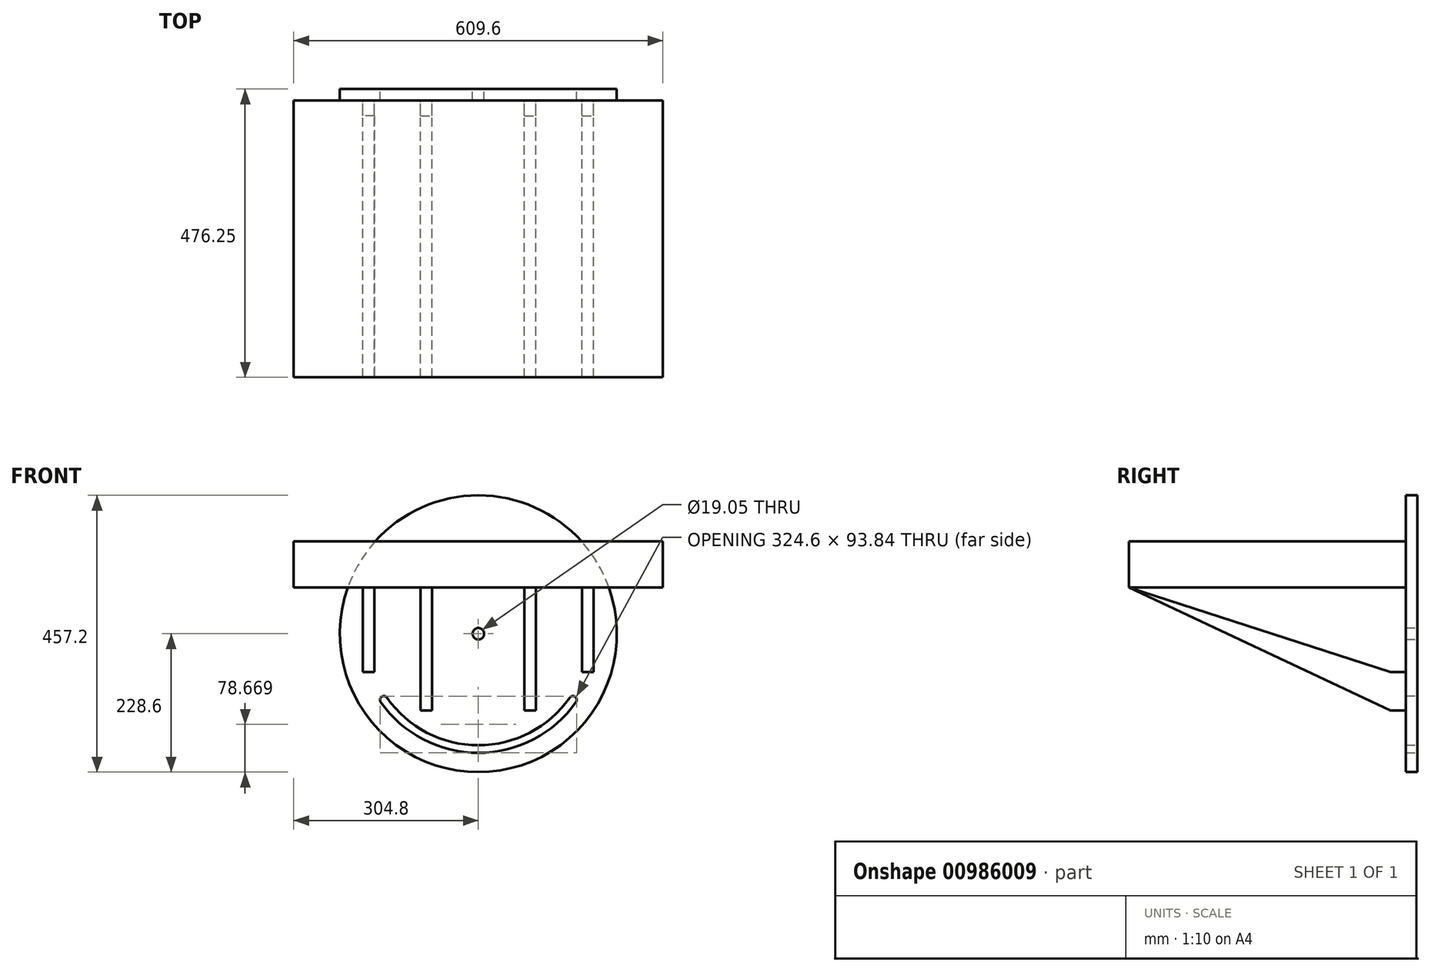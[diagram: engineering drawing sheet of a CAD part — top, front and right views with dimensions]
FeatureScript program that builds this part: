
annotation { "Feature Type Name" : "Feature", "Feature Type Description" : "" }
export const myFeature = defineFeature(function(context is Context, id is Id, definition is map)
    precondition{}
    {
        {
            var Q0;
            Q0=qCreatedBy(makeId("Front.planeOp"),FACE);
            var sketch = newSketch(context, id + "F0", { "sketchPlane" : qUnion([Q0])});
            skCircle(sketch, "E0", {"center": v(0, 0) * mm, "radius": 228.6 * mm});
            skCircle(sketch, "E1", {"center": v(0, 0) * mm, "radius": 9.53 * mm});
            skArc(sketch, "E2.0", {"start": v(-156.05, -109.27) * mm, "mid": v(0, -190.5) * mm, "end": v(156.05, -109.27) * mm});
            skLineSegment(sketch, "E3", {"start": v(0, 0) * mm, "end": v(0, -9.53) * mm});
            skLineSegment(sketch, "E4", {"start": v(0, 0) * mm, "end": v(7.8, -5.46) * mm});
            skLineSegment(sketch, "E5", {"start": v(0, 0) * mm, "end": v(-7.8, -5.46) * mm});
            skArc(sketch, "E6.0.startCap", {"start": v(-161.25, -112.9) * mm, "mid": v(-159.7, -104.06) * mm, "end": v(-150.85, -105.62) * mm});
            skArc(sketch, "E6.0.endCap", {"start": v(150.85, -105.62) * mm, "mid": v(159.7, -104.06) * mm, "end": v(161.25, -112.9) * mm});
            skArc(sketch, "E6.0.left", {"start": v(-150.85, -105.62) * mm, "mid": v(0, -184.15) * mm, "end": v(150.85, -105.62) * mm});
            skArc(sketch, "E6.0.right", {"start": v(-161.25, -112.9) * mm, "mid": v(0, -196.85) * mm, "end": v(161.25, -112.9) * mm});
            skSolve(sketch);
        }
        {
            var Q0;
            Q0=makeQuery(id+"F0.imprint","IMPRINT",FACE,{"disambiguationData":[TD([[makeQuery(id+"F0.imprint","IMPRINT",EDGE,{"derivedFrom":sQuery(id+"F0.wireOp",EDGE,"E0")}),1.0]])]});
            extrude(context, id + "F1", {"entities" : qUnion([Q0]), "depth" : 19.05 * mm, "offsetDistance" : 25.4 * mm});
        }
        {
            var Q0;
            Q0=makeQuery(id+"F1.opExtrude","CAP_FACE",FACE,{"disambiguationData":[OSD([sQuery(id+"F0.wireOp",EDGE,"E0"),sQuery(id+"F0.wireOp",EDGE,"E1"),sQuery(id+"F0.wireOp",EDGE,"E6.0.startCap"),sQuery(id+"F0.wireOp",EDGE,"E6.0.endCap"),sQuery(id+"F0.wireOp",EDGE,"E6.0.left"),sQuery(id+"F0.wireOp",EDGE,"E6.0.right")])],"isStart":false});
            var sketch = newSketch(context, id + "F2", { "sketchPlane" : qUnion([Q0])});
            skLineSegment(sketch, "E7.bottom", {"start": v(-304.8, 152.4) * mm, "end": v(304.8, 152.4) * mm});
            skLineSegment(sketch, "E7.top", {"start": v(-304.8, 76.2) * mm, "end": v(304.8, 76.2) * mm});
            skLineSegment(sketch, "E7.left", {"start": v(-304.8, 152.4) * mm, "end": v(-304.8, 76.2) * mm});
            skLineSegment(sketch, "E7.right", {"start": v(304.8, 152.4) * mm, "end": v(304.8, 76.2) * mm});
            skPoint(sketch, "E7.middle", {"position": v(0, 114.3) * mm});
            skLineSegment(sketch, "E8.bottom", {"start": v(190.5, 76.2) * mm, "end": v(171.45, 76.2) * mm});
            skLineSegment(sketch, "E8.top", {"start": v(190.5, -63.5) * mm, "end": v(171.45, -63.5) * mm});
            skLineSegment(sketch, "E8.left", {"start": v(190.5, 76.2) * mm, "end": v(190.5, -63.5) * mm});
            skLineSegment(sketch, "E8.right", {"start": v(171.45, 76.2) * mm, "end": v(171.45, -63.5) * mm});
            skLineSegment(sketch, "E9.bottom", {"start": v(-190.5, 76.2) * mm, "end": v(-171.45, 76.2) * mm});
            skLineSegment(sketch, "E9.top", {"start": v(-190.5, -63.5) * mm, "end": v(-171.45, -63.5) * mm});
            skLineSegment(sketch, "E9.left", {"start": v(-190.5, 76.2) * mm, "end": v(-190.5, -63.5) * mm});
            skLineSegment(sketch, "E9.right", {"start": v(-171.45, 76.2) * mm, "end": v(-171.45, -63.5) * mm});
            skLineSegment(sketch, "E10.bottom", {"start": v(-95.25, 76.2) * mm, "end": v(-76.2, 76.2) * mm});
            skLineSegment(sketch, "E10.top", {"start": v(-95.25, -127) * mm, "end": v(-76.2, -127) * mm});
            skLineSegment(sketch, "E10.left", {"start": v(-95.25, 76.2) * mm, "end": v(-95.25, -127) * mm});
            skLineSegment(sketch, "E10.right", {"start": v(-76.2, 76.2) * mm, "end": v(-76.2, -127) * mm});
            skLineSegment(sketch, "E11.bottom", {"start": v(95.25, 76.2) * mm, "end": v(76.2, 76.2) * mm});
            skLineSegment(sketch, "E11.top", {"start": v(95.25, -127) * mm, "end": v(76.2, -127) * mm});
            skLineSegment(sketch, "E11.left", {"start": v(95.25, 76.2) * mm, "end": v(95.25, -127) * mm});
            skLineSegment(sketch, "E11.right", {"start": v(76.2, 76.2) * mm, "end": v(76.2, -127) * mm});
            skSolve(sketch);
        }
        {
            var Q0;
            {var subQ0=sQuery(id+"F2.wireOp",EDGE,"E7.right");Q0=makeQuery(id+"F2.imprint","IMPRINT",FACE,{"disambiguationData":[TD([[makeQuery(id+"F2.imprint","IMPRINT",EDGE,{"derivedFrom":subQ0}),-1.0]])]});}
            var Q1;
            {var subQ2=makeQuery(id+"F1.opExtrude","CAP_EDGE",EDGE,{"disambiguationData":[OSD([sQuery(id+"F0.wireOp",EDGE,"E0")])],"isStart":false});var subQ4=sQuery(id+"F2.wireOp",EDGE,"E7.bottom");var subQ14=makeQuery(id+"F2.imprint","INTERSECT",VERTEX,{"disambiguationData":[OD(0.0)],"derivedFrom":[subQ2,subQ4]});Q1=makeQuery(id+"F2.imprint","IMPRINT",FACE,{"disambiguationData":[TD([[makeQuery(id+"F2.imprint","IMPRINT",EDGE,{"disambiguationData":[TD([[subQ14,-1.0]])],"derivedFrom":subQ4}),-1.0]])]});}
            var Q2;
            {var subQ0=sQuery(id+"F2.wireOp",EDGE,"E7.left");Q2=makeQuery(id+"F2.imprint","IMPRINT",FACE,{"disambiguationData":[TD([[makeQuery(id+"F2.imprint","IMPRINT",EDGE,{"derivedFrom":subQ0}),1.0]])]});}
            var Q3;
            Q3=makeQuery(id+"F2.imprint","IMPRINT",FACE,{"disambiguationData":[TD([[makeQuery(id+"F2.imprint","IMPRINT",EDGE,{"derivedFrom":sQuery(id+"F2.wireOp",EDGE,"E9.top")}),1.0]])]});
            var Q4;
            Q4=makeQuery(id+"F2.imprint","IMPRINT",FACE,{"disambiguationData":[TD([[makeQuery(id+"F2.imprint","IMPRINT",EDGE,{"derivedFrom":sQuery(id+"F2.wireOp",EDGE,"E10.top")}),1.0]])]});
            var Q5;
            Q5=makeQuery(id+"F2.imprint","IMPRINT",FACE,{"disambiguationData":[TD([[makeQuery(id+"F2.imprint","IMPRINT",EDGE,{"derivedFrom":sQuery(id+"F2.wireOp",EDGE,"E11.top")}),-1.0]])]});
            var Q6;
            Q6=makeQuery(id+"F2.imprint","IMPRINT",FACE,{"disambiguationData":[TD([[makeQuery(id+"F2.imprint","IMPRINT",EDGE,{"derivedFrom":sQuery(id+"F2.wireOp",EDGE,"E8.top")}),-1.0]])]});
            extrude(context, id + "F3", {"entities" : qUnion([Q0, Q1, Q2, Q3, Q4, Q5, Q6]), "operationType" : NewBodyOperationType.ADD, "depth" : 457.2 * mm, "offsetDistance" : 25.4 * mm});
        }
        {
            var Q0;
            Q0=makeQuery(id+"F3.opExtrude","SWEPT_FACE",FACE,{"disambiguationData":[OSD([sQuery(id+"F2.wireOp",EDGE,"E8.left")])]});
            var sketch = newSketch(context, id + "F4", { "sketchPlane" : qUnion([Q0])});
            skPoint(sketch, "E12", {"position": v(-44.45, -63.5) * mm});
            skLineSegment(sketch, "E13", {"start": v(-476.25, 76.2) * mm, "end": v(-44.45, -63.5) * mm});
            skSolve(sketch);
        }
        {
            var Q0;
            {var subQ0=sQuery(id+"F4.wireOp",EDGE,"E13");Q0=makeQuery(id+"F4.imprint","IMPRINT",FACE,{"disambiguationData":[TD([[makeQuery(id+"F4.imprint","IMPRINT",EDGE,{"derivedFrom":subQ0}),-1.0]])]});}
            extrude(context, id + "F5", {"entities" : qUnion([Q0]), "operationType" : NewBodyOperationType.REMOVE, "oppositeDirection" : true, "depth" : 25.4 * mm, "offsetDistance" : 25.4 * mm});
        }
        {
            var Q0;
            Q0=makeQuery(id+"F3.opExtrude","SWEPT_FACE",FACE,{"disambiguationData":[OSD([sQuery(id+"F2.wireOp",EDGE,"E11.left")])]});
            var sketch = newSketch(context, id + "F6", { "sketchPlane" : qUnion([Q0])});
            skPoint(sketch, "E14", {"position": v(-44.45, -127) * mm});
            skLineSegment(sketch, "E15", {"start": v(-476.25, 76.2) * mm, "end": v(-44.45, -127) * mm});
            skSolve(sketch);
        }
        {
            var Q0;
            {var subQ0=sQuery(id+"F6.wireOp",EDGE,"E15");Q0=makeQuery(id+"F6.imprint","IMPRINT",FACE,{"disambiguationData":[TD([[makeQuery(id+"F6.imprint","IMPRINT",EDGE,{"derivedFrom":subQ0}),-1.0]])]});}
            extrude(context, id + "F7", {"entities" : qUnion([Q0]), "operationType" : NewBodyOperationType.REMOVE, "oppositeDirection" : true, "depth" : 25.4 * mm, "offsetDistance" : 25.4 * mm});
        }
        {
            var Q0;
            Q0=makeQuery(id+"F3.opExtrude","SWEPT_FACE",FACE,{"disambiguationData":[OSD([sQuery(id+"F2.wireOp",EDGE,"E10.right")])]});
            var sketch = newSketch(context, id + "F8", { "sketchPlane" : qUnion([Q0])});
            skPoint(sketch, "E16", {"position": v(-44.45, -127) * mm});
            skLineSegment(sketch, "E17", {"start": v(-476.25, 76.2) * mm, "end": v(-44.45, -127) * mm});
            skSolve(sketch);
        }
        {
            var Q0;
            {var subQ0=sQuery(id+"F8.wireOp",EDGE,"E17");Q0=makeQuery(id+"F8.imprint","IMPRINT",FACE,{"disambiguationData":[TD([[makeQuery(id+"F8.imprint","IMPRINT",EDGE,{"derivedFrom":subQ0}),-1.0]])]});}
            extrude(context, id + "F9", {"entities" : qUnion([Q0]), "operationType" : NewBodyOperationType.REMOVE, "oppositeDirection" : true, "depth" : 25.4 * mm, "offsetDistance" : 25.4 * mm});
        }
        {
            var Q0;
            Q0=makeQuery(id+"F3.opExtrude","SWEPT_FACE",FACE,{"disambiguationData":[OSD([sQuery(id+"F2.wireOp",EDGE,"E9.left")])]});
            var sketch = newSketch(context, id + "F10", { "sketchPlane" : qUnion([Q0])});
            skPoint(sketch, "E18", {"position": v(44.45, -63.5) * mm});
            skLineSegment(sketch, "E19", {"start": v(476.25, 76.2) * mm, "end": v(44.45, -63.5) * mm});
            skSolve(sketch);
        }
        {
            var Q0;
            {var subQ0=sQuery(id+"F10.wireOp",EDGE,"E19");Q0=makeQuery(id+"F10.imprint","IMPRINT",FACE,{"disambiguationData":[TD([[makeQuery(id+"F10.imprint","IMPRINT",EDGE,{"derivedFrom":subQ0}),1.0]])]});}
            extrude(context, id + "F11", {"entities" : qUnion([Q0]), "operationType" : NewBodyOperationType.REMOVE, "oppositeDirection" : true, "depth" : 25.4 * mm, "offsetDistance" : 25.4 * mm});
        }
    });
